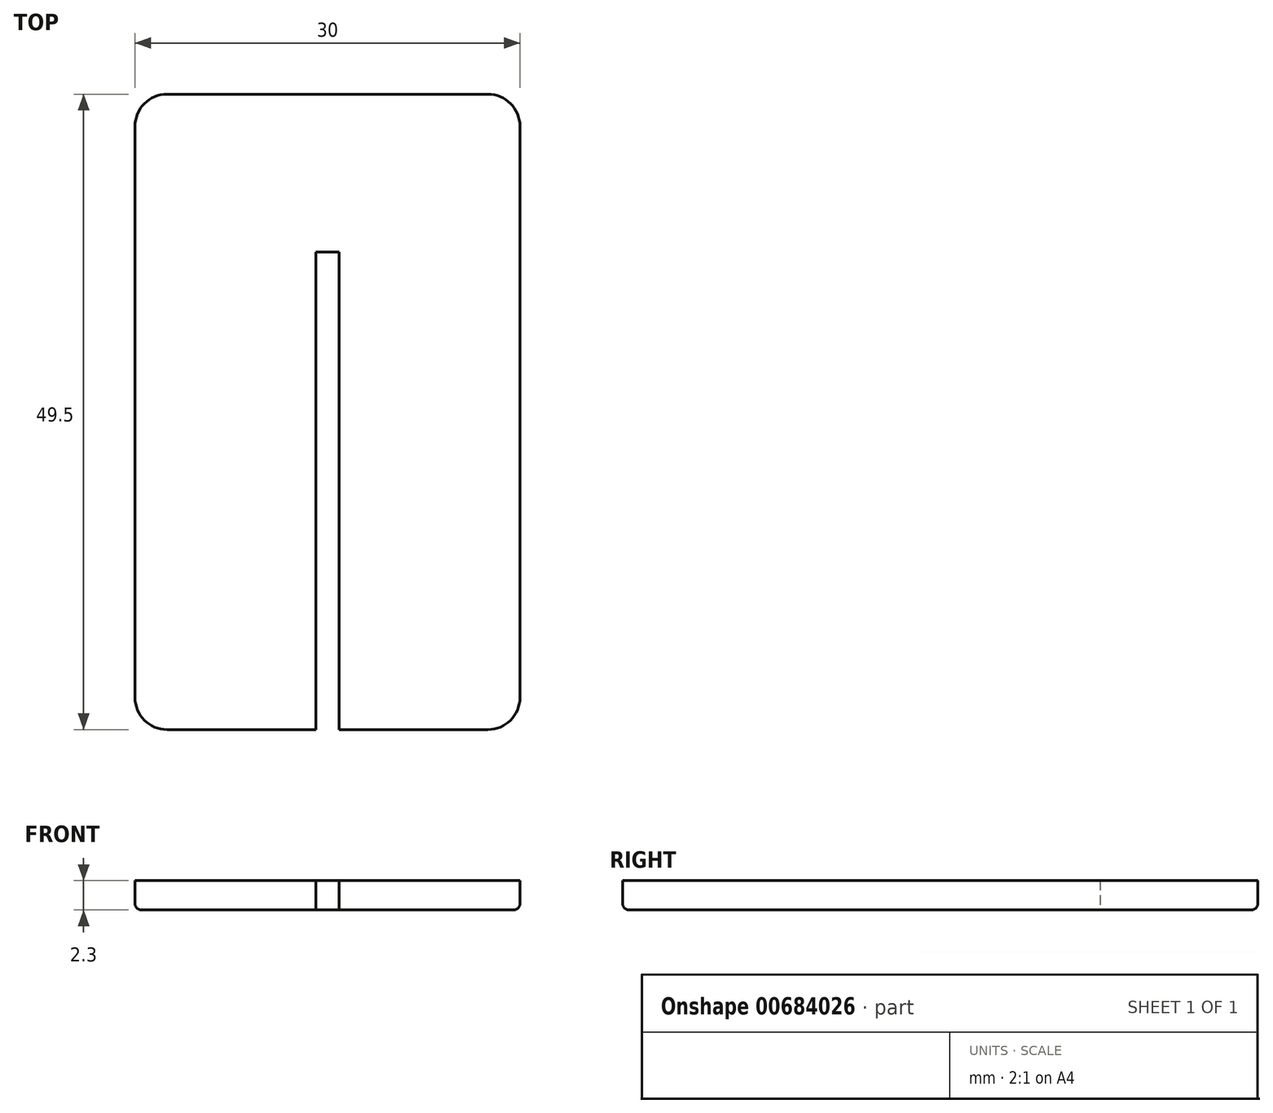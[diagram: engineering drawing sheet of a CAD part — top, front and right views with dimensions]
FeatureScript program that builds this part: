
annotation { "Feature Type Name" : "Feature", "Feature Type Description" : "" }
export const myFeature = defineFeature(function(context is Context, id is Id, definition is map)
    precondition{}
    {
        {
            var Q0;
            Q0=qCreatedBy(makeId("Top.planeOp"),FACE);
            var sketch = newSketch(context, id + "F0", { "sketchPlane" : qUnion([Q0])});
            skLineSegment(sketch, "E0.bottom", {"start": v(-15, 24.75) * mm, "end": v(15, 24.75) * mm});
            skLineSegment(sketch, "E0.top", {"start": v(-15, -24.75) * mm, "end": v(-0.9, -24.75) * mm});
            skLineSegment(sketch, "E0.left", {"start": v(-15, 24.75) * mm, "end": v(-15, -24.75) * mm});
            skLineSegment(sketch, "E0.right", {"start": v(15, 24.75) * mm, "end": v(15, -24.75) * mm});
            skPoint(sketch, "E0.middle", {"position": v(0, 0) * mm});
            skLineSegment(sketch, "E1.top", {"start": v(0.9, 12.45) * mm, "end": v(-0.9, 12.45) * mm});
            skLineSegment(sketch, "E1.left", {"start": v(0.9, -24.75) * mm, "end": v(0.9, 12.45) * mm});
            skLineSegment(sketch, "E1.right", {"start": v(-0.9, -24.75) * mm, "end": v(-0.9, 12.45) * mm});
            skLineSegment(sketch, "E2.trimOffspring", {"start": v(0.9, -24.75) * mm, "end": v(15, -24.75) * mm});
            skSolve(sketch);
        }
        {
            var Q0;
            Q0 = qSketchRegion(id + "F0", true);
            extrude(context, id + "F1", {"entities" : qUnion([Q0]), "depth" : 2.3 * mm, "offsetDistance" : 25 * mm});
        }
        {
            var Q0;
            Q0=makeQuery(id+"F1.opExtrude","SWEPT_EDGE",EDGE,{"disambiguationData":[OSD([sQuery(id+"F0.wireOp",EDGE,"E0.bottom"),sQuery(id+"F0.wireOp",EDGE,"E0.left")])]});
            var Q1;
            Q1=makeQuery(id+"F1.opExtrude","SWEPT_EDGE",EDGE,{"disambiguationData":[OSD([sQuery(id+"F0.wireOp",EDGE,"E0.top"),sQuery(id+"F0.wireOp",EDGE,"E0.left")])]});
            var Q2;
            Q2=makeQuery(id+"F1.opExtrude","SWEPT_EDGE",EDGE,{"disambiguationData":[OSD([sQuery(id+"F0.wireOp",EDGE,"E0.right"),sQuery(id+"F0.wireOp",EDGE,"E2.trimOffspring")])]});
            var Q3;
            Q3=makeQuery(id+"F1.opExtrude","SWEPT_EDGE",EDGE,{"disambiguationData":[OSD([sQuery(id+"F0.wireOp",EDGE,"E0.bottom"),sQuery(id+"F0.wireOp",EDGE,"E0.right")])]});
            fillet(context, id + "F2", {"entities" : qUnion([Q0, Q1, Q2, Q3]), "radius" : 2.5 * mm, "tangentPropagation" : true, "allowEdgeOverflow" : false});
        }
        {
            var Q0;
            Q0=makeQuery(id+"F1.opExtrude","CAP_EDGE",EDGE,{"disambiguationData":[OSD([sQuery(id+"F0.wireOp",EDGE,"E2.trimOffspring")])],"isStart":true});
            var Q1;
            {var subQ0=sQuery(id+"F0.wireOp",EDGE,"E2.trimOffspring");var subQ1=sQuery(id+"F0.wireOp",EDGE,"E0.right");Q1=makeQuery(id+"F2.opFillet","BLEND_EDGE",EDGE,{"blendedFrom":[makeQuery(id+"F1.opExtrude","SWEPT_EDGE",EDGE,{"disambiguationData":[OSD([subQ1,subQ0])]}),makeQuery(id+"F1.opExtrude","CAP_FACE",FACE,{"disambiguationData":[OSD([sQuery(id+"F0.wireOp",EDGE,"E0.bottom"),sQuery(id+"F0.wireOp",EDGE,"E0.top"),sQuery(id+"F0.wireOp",EDGE,"E0.left"),subQ1,sQuery(id+"F0.wireOp",EDGE,"E1.top"),sQuery(id+"F0.wireOp",EDGE,"E1.left"),sQuery(id+"F0.wireOp",EDGE,"E1.right"),subQ0])],"isStart":true})],"blendedInto":[makeQuery(id+"F1.opExtrude","CAP_FACE",FACE,{"disambiguationData":[OSD([sQuery(id+"F0.wireOp",EDGE,"E0.bottom"),sQuery(id+"F0.wireOp",EDGE,"E0.top"),sQuery(id+"F0.wireOp",EDGE,"E0.left"),subQ1,sQuery(id+"F0.wireOp",EDGE,"E1.top"),sQuery(id+"F0.wireOp",EDGE,"E1.left"),sQuery(id+"F0.wireOp",EDGE,"E1.right"),subQ0])],"isStart":true})]});}
            var Q2;
            Q2=makeQuery(id+"F1.opExtrude","CAP_EDGE",EDGE,{"disambiguationData":[OSD([sQuery(id+"F0.wireOp",EDGE,"E0.right")])],"isStart":true});
            var Q3;
            Q3=makeQuery(id+"F1.opExtrude","CAP_EDGE",EDGE,{"disambiguationData":[OSD([sQuery(id+"F0.wireOp",EDGE,"E0.bottom")])],"isStart":true});
            var Q4;
            {var subQ0=sQuery(id+"F0.wireOp",EDGE,"E0.right");var subQ1=sQuery(id+"F0.wireOp",EDGE,"E0.bottom");Q4=makeQuery(id+"F2.opFillet","BLEND_EDGE",EDGE,{"blendedFrom":[makeQuery(id+"F1.opExtrude","SWEPT_EDGE",EDGE,{"disambiguationData":[OSD([subQ1,subQ0])]}),makeQuery(id+"F1.opExtrude","CAP_FACE",FACE,{"disambiguationData":[OSD([subQ1,sQuery(id+"F0.wireOp",EDGE,"E0.top"),sQuery(id+"F0.wireOp",EDGE,"E0.left"),subQ0,sQuery(id+"F0.wireOp",EDGE,"E1.top"),sQuery(id+"F0.wireOp",EDGE,"E1.left"),sQuery(id+"F0.wireOp",EDGE,"E1.right"),sQuery(id+"F0.wireOp",EDGE,"E2.trimOffspring")])],"isStart":true})],"blendedInto":[makeQuery(id+"F1.opExtrude","CAP_FACE",FACE,{"disambiguationData":[OSD([subQ1,sQuery(id+"F0.wireOp",EDGE,"E0.top"),sQuery(id+"F0.wireOp",EDGE,"E0.left"),subQ0,sQuery(id+"F0.wireOp",EDGE,"E1.top"),sQuery(id+"F0.wireOp",EDGE,"E1.left"),sQuery(id+"F0.wireOp",EDGE,"E1.right"),sQuery(id+"F0.wireOp",EDGE,"E2.trimOffspring")])],"isStart":true})]});}
            var Q5;
            {var subQ0=sQuery(id+"F0.wireOp",EDGE,"E0.left");var subQ1=sQuery(id+"F0.wireOp",EDGE,"E0.bottom");Q5=makeQuery(id+"F2.opFillet","BLEND_EDGE",EDGE,{"blendedFrom":[makeQuery(id+"F1.opExtrude","SWEPT_EDGE",EDGE,{"disambiguationData":[OSD([subQ1,subQ0])]}),makeQuery(id+"F1.opExtrude","CAP_FACE",FACE,{"disambiguationData":[OSD([subQ1,sQuery(id+"F0.wireOp",EDGE,"E0.top"),subQ0,sQuery(id+"F0.wireOp",EDGE,"E0.right"),sQuery(id+"F0.wireOp",EDGE,"E1.top"),sQuery(id+"F0.wireOp",EDGE,"E1.left"),sQuery(id+"F0.wireOp",EDGE,"E1.right"),sQuery(id+"F0.wireOp",EDGE,"E2.trimOffspring")])],"isStart":true})],"blendedInto":[makeQuery(id+"F1.opExtrude","CAP_FACE",FACE,{"disambiguationData":[OSD([subQ1,sQuery(id+"F0.wireOp",EDGE,"E0.top"),subQ0,sQuery(id+"F0.wireOp",EDGE,"E0.right"),sQuery(id+"F0.wireOp",EDGE,"E1.top"),sQuery(id+"F0.wireOp",EDGE,"E1.left"),sQuery(id+"F0.wireOp",EDGE,"E1.right"),sQuery(id+"F0.wireOp",EDGE,"E2.trimOffspring")])],"isStart":true})]});}
            var Q6;
            Q6=makeQuery(id+"F1.opExtrude","CAP_EDGE",EDGE,{"disambiguationData":[OSD([sQuery(id+"F0.wireOp",EDGE,"E0.left")])],"isStart":true});
            var Q7;
            {var subQ0=sQuery(id+"F0.wireOp",EDGE,"E0.left");var subQ1=sQuery(id+"F0.wireOp",EDGE,"E0.top");Q7=makeQuery(id+"F2.opFillet","BLEND_EDGE",EDGE,{"blendedFrom":[makeQuery(id+"F1.opExtrude","SWEPT_EDGE",EDGE,{"disambiguationData":[OSD([subQ1,subQ0])]}),makeQuery(id+"F1.opExtrude","CAP_FACE",FACE,{"disambiguationData":[OSD([sQuery(id+"F0.wireOp",EDGE,"E0.bottom"),subQ1,subQ0,sQuery(id+"F0.wireOp",EDGE,"E0.right"),sQuery(id+"F0.wireOp",EDGE,"E1.top"),sQuery(id+"F0.wireOp",EDGE,"E1.left"),sQuery(id+"F0.wireOp",EDGE,"E1.right"),sQuery(id+"F0.wireOp",EDGE,"E2.trimOffspring")])],"isStart":true})],"blendedInto":[makeQuery(id+"F1.opExtrude","CAP_FACE",FACE,{"disambiguationData":[OSD([sQuery(id+"F0.wireOp",EDGE,"E0.bottom"),subQ1,subQ0,sQuery(id+"F0.wireOp",EDGE,"E0.right"),sQuery(id+"F0.wireOp",EDGE,"E1.top"),sQuery(id+"F0.wireOp",EDGE,"E1.left"),sQuery(id+"F0.wireOp",EDGE,"E1.right"),sQuery(id+"F0.wireOp",EDGE,"E2.trimOffspring")])],"isStart":true})]});}
            fillet(context, id + "F3", {"entities" : qUnion([Q0, Q1, Q2, Q3, Q4, Q5, Q6, Q7]), "radius" : 0.5 * mm, "tangentPropagation" : true, "allowEdgeOverflow" : false});
        }
    });
